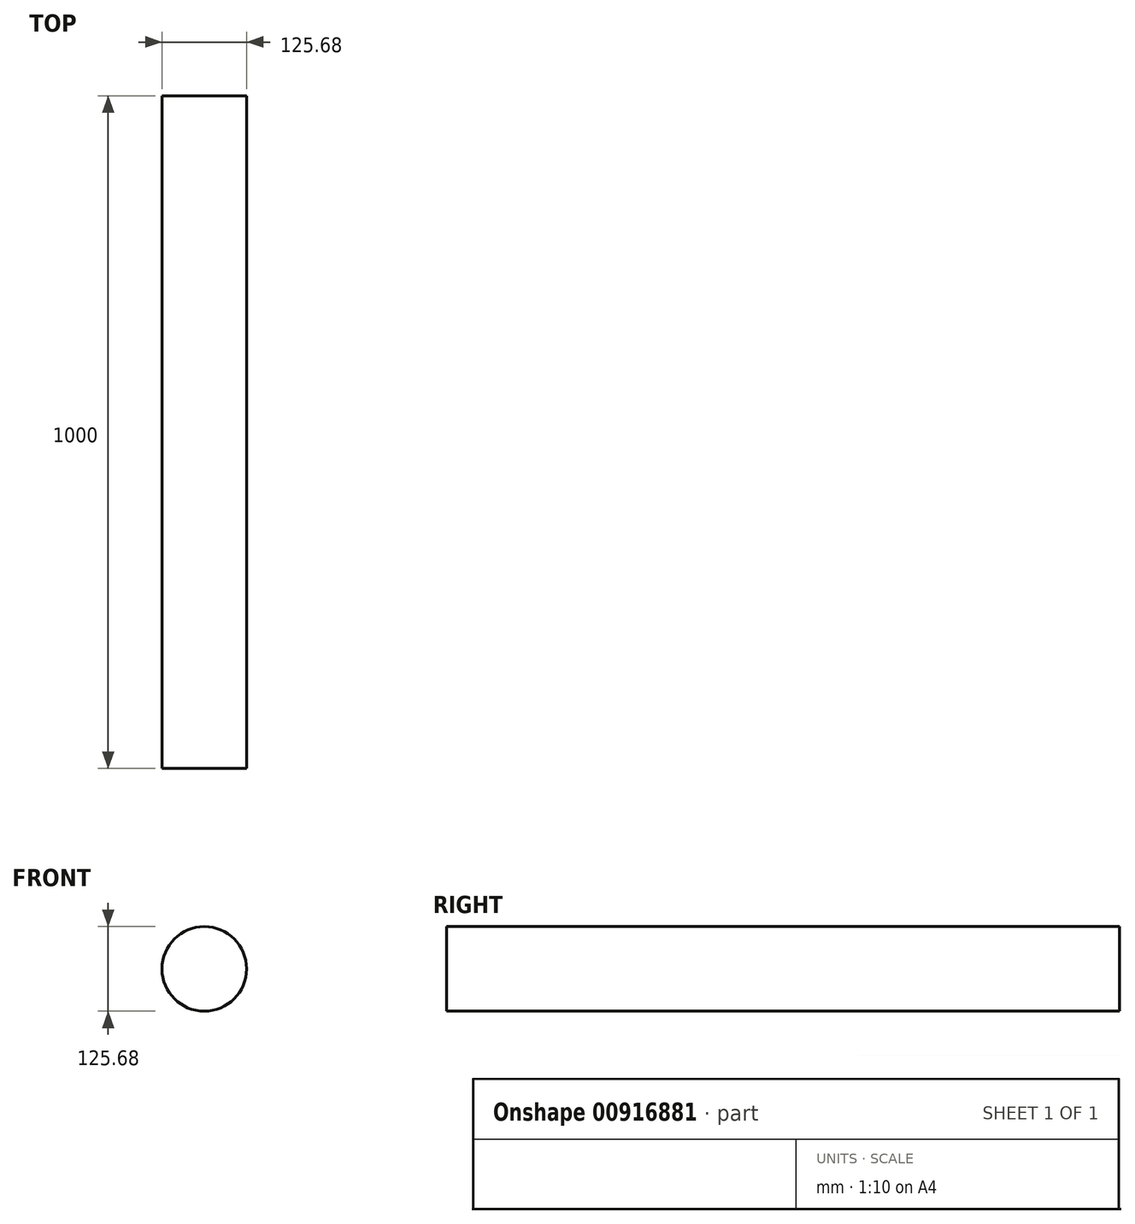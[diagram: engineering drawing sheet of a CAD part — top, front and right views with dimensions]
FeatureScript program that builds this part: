
annotation { "Feature Type Name" : "Feature", "Feature Type Description" : "" }
export const myFeature = defineFeature(function(context is Context, id is Id, definition is map)
    precondition{}
    {
        {
            var Q0;
            Q0=qCreatedBy(makeId("Front.planeOp"),FACE);
            var sketch = newSketch(context, id + "F0", { "sketchPlane" : qUnion([Q0])});
            skCircle(sketch, "E0", {"center": v(0, 0) * mm, "radius": 62.84 * mm});
            skSolve(sketch);
        }
        {
            var Q0;
            Q0=makeQuery(id+"F0.imprint","IMPRINT",FACE,{"disambiguationData":[TD([[makeQuery(id+"F0.imprint","IMPRINT",EDGE,{"derivedFrom":sQuery(id+"F0.wireOp",EDGE,"E0")}),1.0]])]});
            extrude(context, id + "F1", {"entities" : qUnion([Q0]), "depth" : 1000 * mm, "offsetDistance" : 25.4 * mm});
        }
    });
